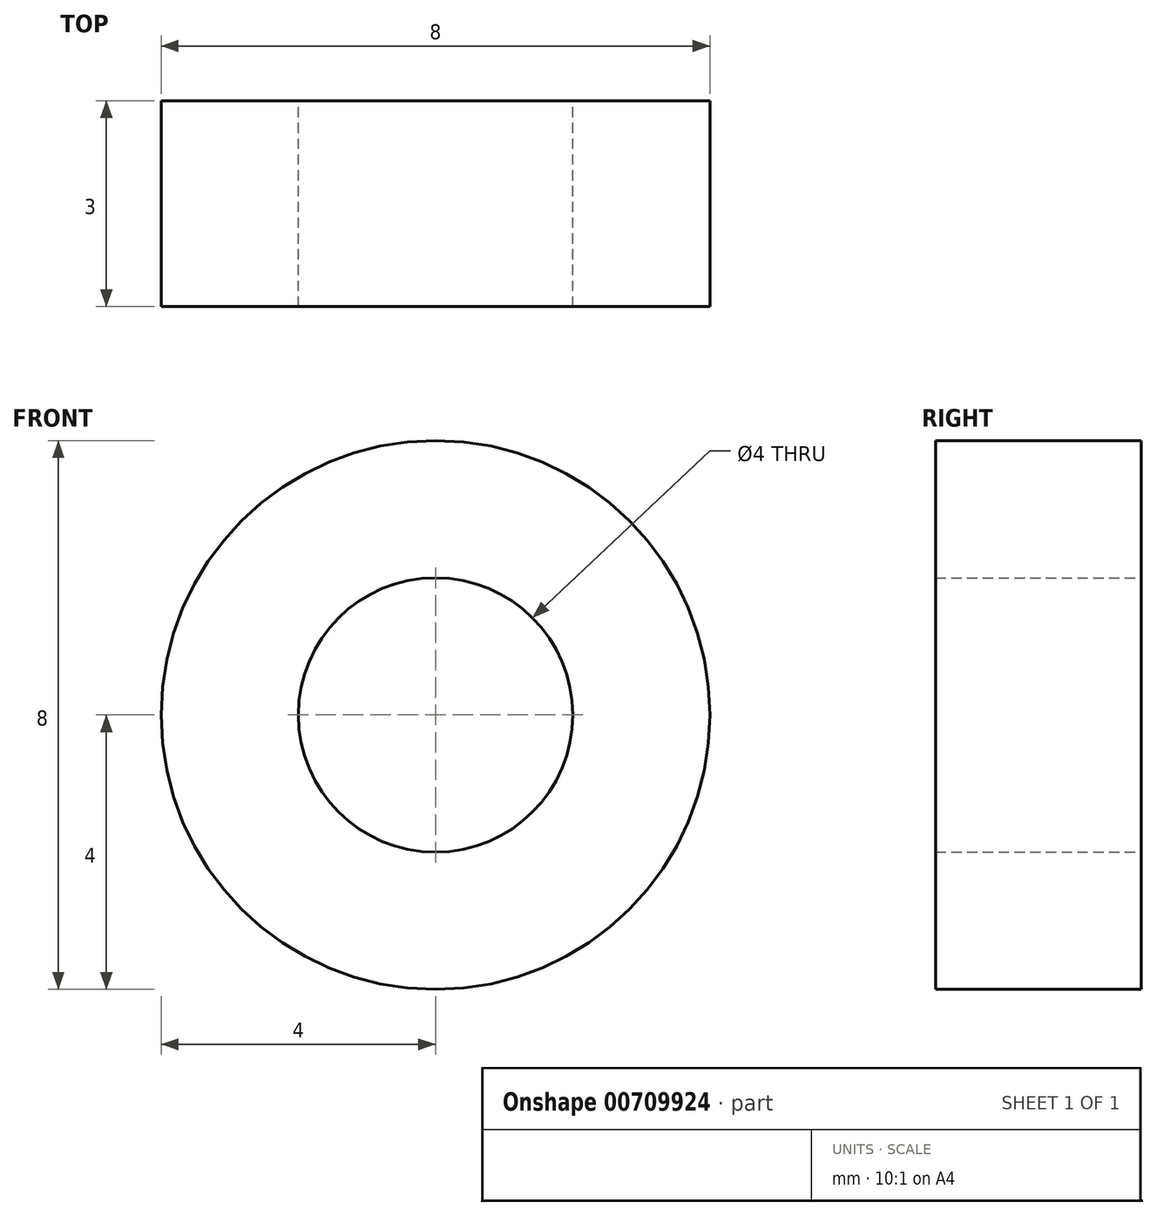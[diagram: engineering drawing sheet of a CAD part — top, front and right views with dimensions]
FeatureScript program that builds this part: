
annotation { "Feature Type Name" : "Feature", "Feature Type Description" : "" }
export const myFeature = defineFeature(function(context is Context, id is Id, definition is map)
    precondition{}
    {
        {
            var Q0;
            Q0=qCreatedBy(makeId("Front.planeOp"),FACE);
            var sketch = newSketch(context, id + "F0", { "sketchPlane" : qUnion([Q0])});
            skCircle(sketch, "E0", {"center": v(0, 0) * mm, "radius": 4 * mm});
            skCircle(sketch, "E1", {"center": v(0, 0) * mm, "radius": 2 * mm});
            skSolve(sketch);
        }
        {
            var Q0;
            Q0=makeQuery(id+"F0.imprint","IMPRINT",FACE,{"disambiguationData":[TD([[makeQuery(id+"F0.imprint","IMPRINT",EDGE,{"derivedFrom":sQuery(id+"F0.wireOp",EDGE,"E0")}),1.0]])]});
            extrude(context, id + "F1", {"entities" : qUnion([Q0]), "depth" : 3 * mm, "offsetDistance" : 25 * mm});
        }
    });
